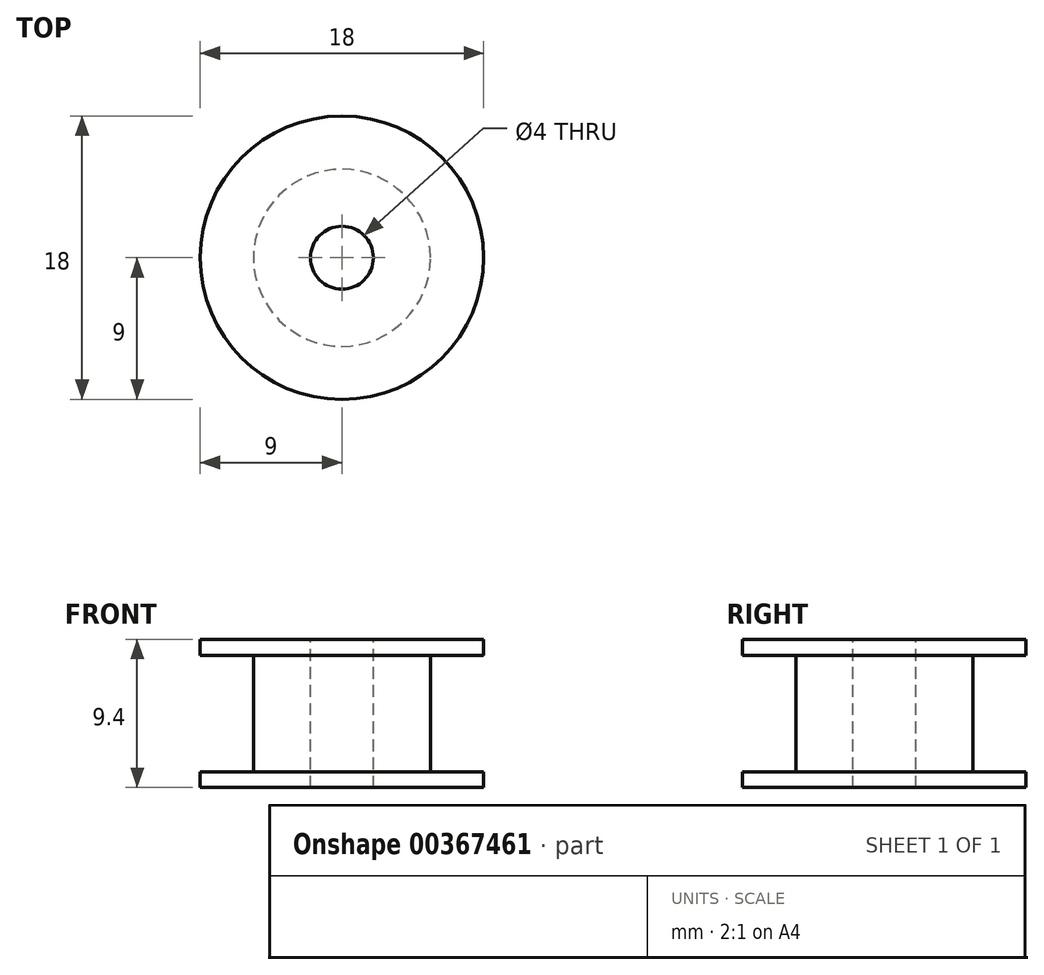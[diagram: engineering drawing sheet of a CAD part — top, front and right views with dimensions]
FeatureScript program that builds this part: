
annotation { "Feature Type Name" : "Feature", "Feature Type Description" : "" }
export const myFeature = defineFeature(function(context is Context, id is Id, definition is map)
    precondition{}
    {
        {
            var Q0;
            Q0=qCreatedBy(makeId("Top.planeOp"),FACE);
            var sketch = newSketch(context, id + "F0", { "sketchPlane" : qUnion([Q0])});
            skCircle(sketch, "E0", {"center": v(0, 0) * mm, "radius": 9 * mm});
            skSolve(sketch);
        }
        {
            var Q0;
            Q0=qSketchRegion(id+"F0",true);
            extrude(context, id + "F1", {"entities" : qUnion([Q0]), "depth" : 1 * mm});
        }
        {
            var Q0;
            Q0=makeQuery(id+"F1.opExtrude","CAP_FACE",FACE,{"disambiguationData":[OSD([sQuery(id+"F0.wireOp",EDGE,"E0")])],"isStart":false});
            var sketch = newSketch(context, id + "F2", { "sketchPlane" : qUnion([Q0])});
            skCircle(sketch, "E1", {"center": v(0, 0) * mm, "radius": 5.62 * mm});
            skSolve(sketch);
        }
        {
            var Q0;
            Q0=qSketchRegion(id+"F2",true);
            extrude(context, id + "F3", {"entities" : qUnion([Q0]), "operationType" : NewBodyOperationType.ADD, "depth" : 7.4 * mm});
        }
        {
            var Q0;
            Q0=makeQuery(id+"F3.opExtrude","CAP_FACE",FACE,{"disambiguationData":[OSD([sQuery(id+"F2.wireOp",EDGE,"E1")])],"isStart":false});
            var sketch = newSketch(context, id + "F4", { "sketchPlane" : qUnion([Q0])});
            skCircle(sketch, "E2", {"center": v(0, 0) * mm, "radius": 9 * mm});
            skSolve(sketch);
        }
        {
            var Q0;
            Q0=qSketchRegion(id+"F4",true);
            extrude(context, id + "F5", {"entities" : qUnion([Q0]), "operationType" : NewBodyOperationType.ADD, "depth" : 1 * mm});
        }
        {
            var Q0;
            Q0=makeQuery(id+"F5.opExtrude","CAP_FACE",FACE,{"disambiguationData":[OSD([sQuery(id+"F4.wireOp",EDGE,"E2")])],"isStart":false});
            var sketch = newSketch(context, id + "F6", { "sketchPlane" : qUnion([Q0])});
            skPoint(sketch, "E3", {"position": v(0, 0) * mm});
            skSolve(sketch);
        }
        {
            var Q0;
            Q0=sQuery(id+"F6.wireOp",VERTEX,"E3");
            var Q1;
            Q1=makeQuery(id+"F1.opExtrude","SWEPT_BODY",BODY,{"disambiguationData":[OSD([sQuery(id+"F0.wireOp",EDGE,"E0")])]});
            hole(context, id + "F7", {"style" : HoleStyle.SIMPLE, "endStyle" : HoleEndStyle.THROUGH, "holeDiameter" : 4 * mm, "locations" : qUnion([Q0]), "scope" : qUnion([Q1]), "isTappedThrough" : true});
        }
    });
